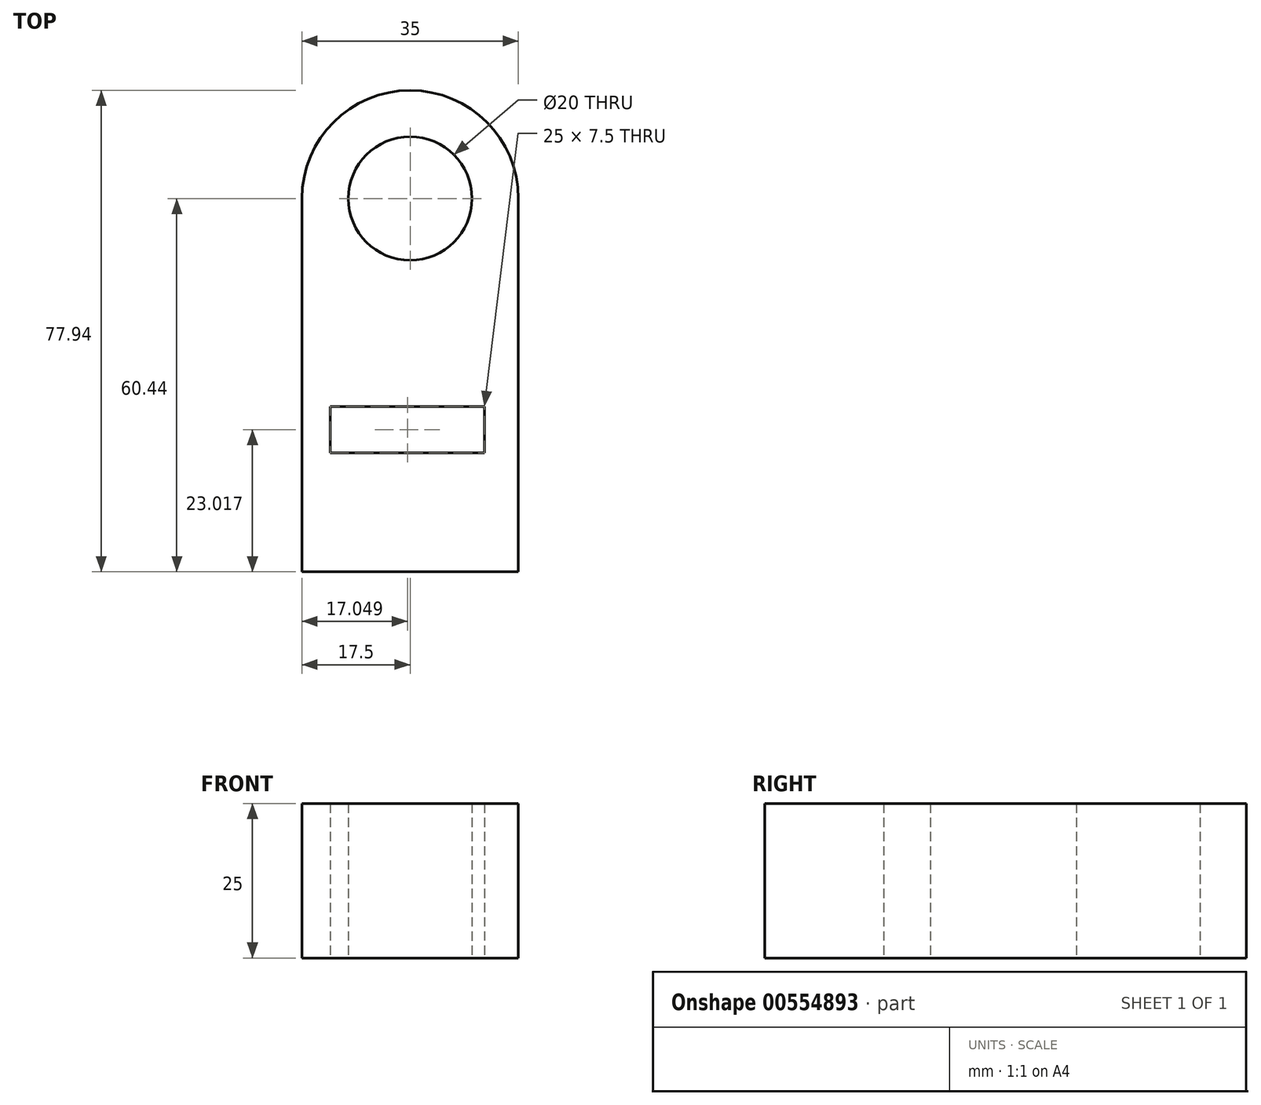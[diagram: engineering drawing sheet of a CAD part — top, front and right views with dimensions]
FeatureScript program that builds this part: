
annotation { "Feature Type Name" : "Feature", "Feature Type Description" : "" }
export const myFeature = defineFeature(function(context is Context, id is Id, definition is map)
    precondition{}
    {
        {
            var Q0;
            Q0=qCreatedBy(makeId("Top.planeOp"),FACE);
            var sketch = newSketch(context, id + "F0", { "sketchPlane" : qUnion([Q0])});
            skCircle(sketch, "E0", {"center": v(0, 0) * mm, "radius": 10 * mm});
            skCircle(sketch, "E1", {"center": v(0, 0) * mm, "radius": 17.5 * mm});
            skLineSegment(sketch, "E2", {"start": v(-17.5, 0) * mm, "end": v(-17.5, -60.44) * mm});
            skLineSegment(sketch, "E3", {"start": v(-17.5, -60.44) * mm, "end": v(17.5, -60.44) * mm});
            skLineSegment(sketch, "E4", {"start": v(17.5, 0) * mm, "end": v(17.5, -60.44) * mm});
            skLineSegment(sketch, "E5", {"start": v(-12.95, -33.67) * mm, "end": v(12.05, -33.67) * mm});
            skLineSegment(sketch, "E6", {"start": v(12.05, -33.67) * mm, "end": v(12.05, -41.17) * mm});
            skLineSegment(sketch, "E7", {"start": v(12.05, -41.17) * mm, "end": v(-12.95, -41.17) * mm});
            skLineSegment(sketch, "E8", {"start": v(-12.95, -41.17) * mm, "end": v(-12.95, -33.67) * mm});
            skSolve(sketch);
        }
        {
            var Q0;
            Q0 = qSketchRegion(id + "F0", true);
            extrude(context, id + "F1", {"entities" : qUnion([Q0]), "depth" : 25 * mm, "offsetDistance" : 25 * mm});
        }
    });
